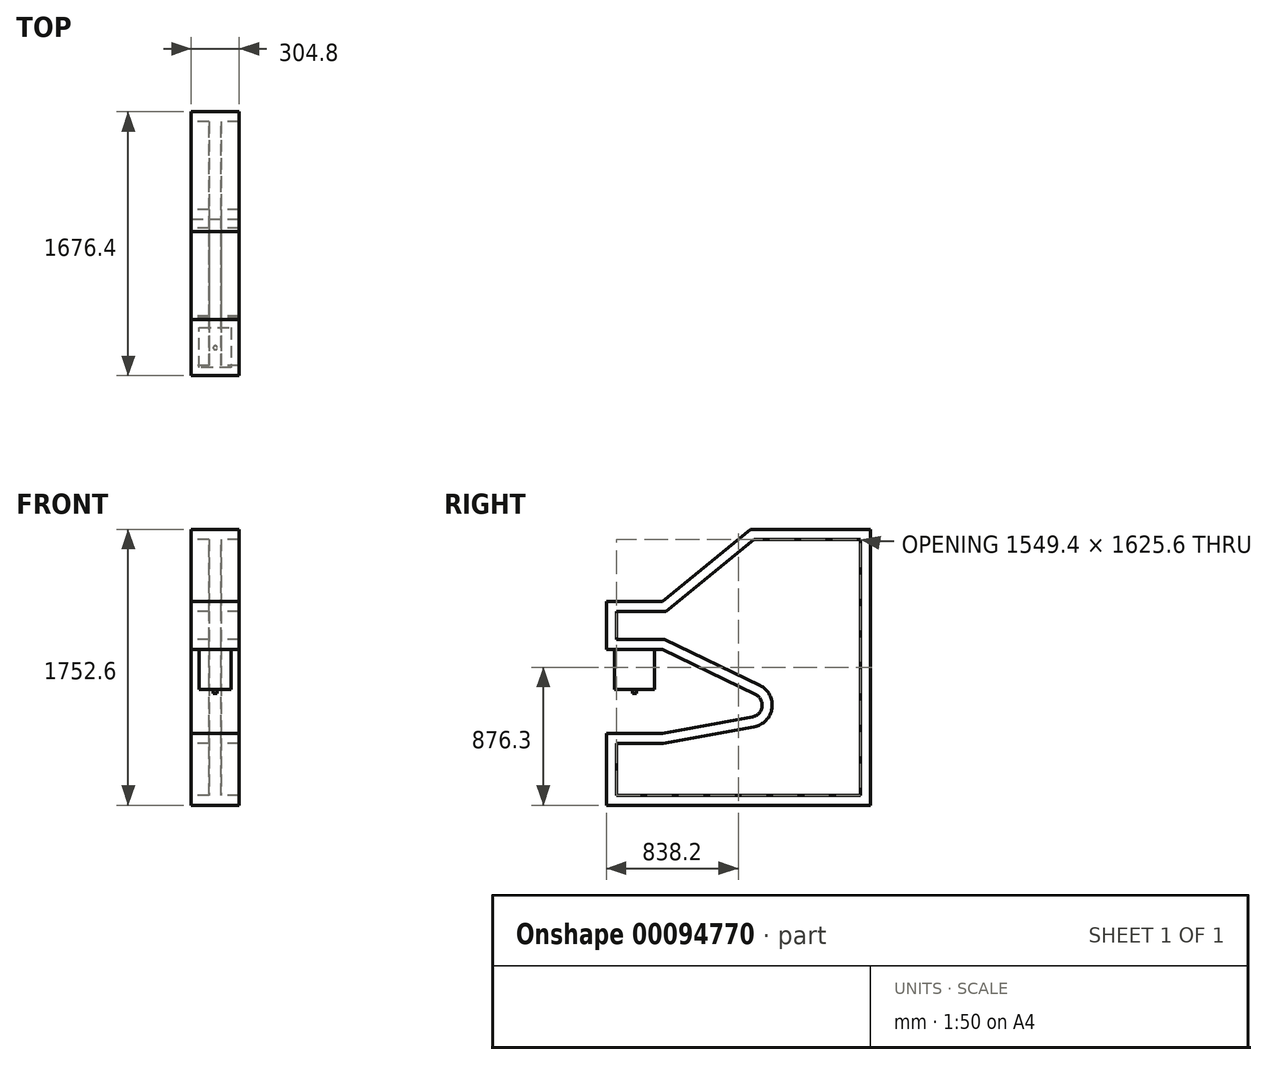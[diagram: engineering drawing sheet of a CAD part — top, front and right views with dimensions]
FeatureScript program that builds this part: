
annotation { "Feature Type Name" : "Feature", "Feature Type Description" : "" }
export const myFeature = defineFeature(function(context is Context, id is Id, definition is map)
    precondition{}
    {
        {
            var Q0;
            Q0=qCreatedBy(makeId("Right.planeOp"),FACE);
            var sketch = newSketch(context, id + "F0", { "sketchPlane" : qUnion([Q0])});
            skLineSegment(sketch, "E0", {"start": v(-914.4, 0) * mm, "end": v(762, 0) * mm, "construction": true});
            skLineSegment(sketch, "E1.0", {"start": v(-914.4, 457.2) * mm, "end": v(0, 457.2) * mm, "construction": true});
            skLineSegment(sketch, "E2.0", {"start": v(-1354.22, 635) * mm, "end": v(1358.95, 635) * mm, "construction": true});
            skLineSegment(sketch, "E3.0", {"start": v(-914.4, 990.6) * mm, "end": v(0, 990.6) * mm, "construction": true});
            skLineSegment(sketch, "E4.0", {"start": v(-914.4, 1295.4) * mm, "end": v(0, 1295.4) * mm, "construction": true});
            skLineSegment(sketch, "E5", {"start": v(-914.4, 1295.4) * mm, "end": v(-914.4, 0) * mm, "construction": true});
            skLineSegment(sketch, "E6.0", {"start": v(-558.8, 1295.4) * mm, "end": v(-558.8, 0) * mm, "construction": true});
            skLineSegment(sketch, "E7.0", {"start": v(-1354.22, 1752.6) * mm, "end": v(1358.95, 1752.6) * mm, "construction": true});
            skLineSegment(sketch, "E8", {"start": v(0, -258.78) * mm, "end": v(0, 1895.33) * mm, "construction": true});
            skLineSegment(sketch, "E9.0", {"start": v(762, -258.78) * mm, "end": v(762, 1895.33) * mm, "construction": true});
            skArc(sketch, "E10", {"start": v(13.47, 560) * mm, "mid": v(75.49, 624.6) * mm, "end": v(33.24, 703.57) * mm});
            skLineSegment(sketch, "E11", {"start": v(-558.8, 990.6) * mm, "end": v(33.24, 703.57) * mm});
            skLineSegment(sketch, "E12", {"start": v(-558.8, 457.2) * mm, "end": v(13.47, 560) * mm});
            skLineSegment(sketch, "E13", {"start": v(-558.8, 990.6) * mm, "end": v(-914.4, 990.6) * mm});
            skLineSegment(sketch, "E14", {"start": v(-914.4, 990.6) * mm, "end": v(-914.4, 1295.4) * mm});
            skLineSegment(sketch, "E15", {"start": v(-914.4, 1295.4) * mm, "end": v(-558.8, 1295.4) * mm});
            skLineSegment(sketch, "E16", {"start": v(-558.8, 1295.4) * mm, "end": v(0, 1752.6) * mm});
            skLineSegment(sketch, "E17", {"start": v(0, 1752.6) * mm, "end": v(762, 1752.6) * mm});
            skLineSegment(sketch, "E18", {"start": v(762, 1752.6) * mm, "end": v(762, 0) * mm});
            skLineSegment(sketch, "E19", {"start": v(-914.4, 0) * mm, "end": v(762, 0) * mm});
            skLineSegment(sketch, "E20", {"start": v(-914.4, 0) * mm, "end": v(-914.4, 457.2) * mm});
            skLineSegment(sketch, "E21", {"start": v(-914.4, 457.2) * mm, "end": v(-558.8, 457.2) * mm});
            skPoint(sketch, "E22.orphan", {"position": v(0, 557.58) * mm});
            skSolve(sketch);
        }
        {
            var Q0;
            Q0=qSketchRegion(id+"F0",true);
            extrude(context, id + "F1", {"entities" : qUnion([Q0]), "endBound" : BoundingType.SYMMETRIC, "depth" : 76.2 * mm});
        }
        {
            var Q0;
            Q0=qCreatedBy(makeId("Right.planeOp"),FACE);
            var sketch = newSketch(context, id + "F2", { "sketchPlane" : qUnion([Q0])});
            skArc(sketch, "E23.0.0", {"start": v(33.24, 703.57) * mm, "mid": v(75.49, 624.6) * mm, "end": v(13.47, 560) * mm});
            skLineSegment(sketch, "E23.0.1", {"start": v(13.47, 560) * mm, "end": v(-558.8, 457.2) * mm});
            skLineSegment(sketch, "E23.0.2", {"start": v(-558.8, 457.2) * mm, "end": v(-914.4, 457.2) * mm});
            skLineSegment(sketch, "E23.0.3", {"start": v(-914.4, 457.2) * mm, "end": v(-914.4, 0) * mm});
            skLineSegment(sketch, "E23.0.4", {"start": v(-914.4, 0) * mm, "end": v(762, 0) * mm});
            skLineSegment(sketch, "E23.0.5", {"start": v(762, 0) * mm, "end": v(762, 1752.6) * mm});
            skLineSegment(sketch, "E23.0.6", {"start": v(762, 1752.6) * mm, "end": v(0, 1752.6) * mm});
            skLineSegment(sketch, "E23.0.7", {"start": v(0, 1752.6) * mm, "end": v(-558.8, 1295.4) * mm});
            skLineSegment(sketch, "E23.0.8", {"start": v(-558.8, 1295.4) * mm, "end": v(-914.4, 1295.4) * mm});
            skLineSegment(sketch, "E23.0.9", {"start": v(-914.4, 1295.4) * mm, "end": v(-914.4, 990.6) * mm});
            skLineSegment(sketch, "E23.0.10", {"start": v(-914.4, 990.6) * mm, "end": v(-558.8, 990.6) * mm});
            skLineSegment(sketch, "E23.0.11", {"start": v(-558.8, 990.6) * mm, "end": v(33.24, 703.57) * mm});
            skLineSegment(sketch, "E24.0", {"start": v(698.5, 63.5) * mm, "end": v(698.5, 1689.1) * mm});
            skLineSegment(sketch, "E24.1", {"start": v(-850.9, 1054.1) * mm, "end": v(-544.22, 1054.1) * mm});
            skLineSegment(sketch, "E24.2", {"start": v(-850.9, 1231.9) * mm, "end": v(-850.9, 1054.1) * mm});
            skLineSegment(sketch, "E24.3", {"start": v(-536.13, 1231.9) * mm, "end": v(-850.9, 1231.9) * mm});
            skLineSegment(sketch, "E24.4", {"start": v(22.67, 1689.1) * mm, "end": v(-536.13, 1231.9) * mm});
            skLineSegment(sketch, "E24.5", {"start": v(-544.22, 1054.1) * mm, "end": v(60.94, 760.7) * mm});
            skLineSegment(sketch, "E24.6", {"start": v(698.5, 1689.1) * mm, "end": v(22.67, 1689.1) * mm});
            skArc(sketch, "E24.7", {"start": v(60.94, 760.7) * mm, "mid": v(138.4, 615.94) * mm, "end": v(24.7, 497.5) * mm});
            skLineSegment(sketch, "E24.8", {"start": v(24.7, 497.5) * mm, "end": v(-553.14, 393.7) * mm});
            skLineSegment(sketch, "E24.9", {"start": v(-553.14, 393.7) * mm, "end": v(-850.9, 393.7) * mm});
            skLineSegment(sketch, "E24.10", {"start": v(-850.9, 393.7) * mm, "end": v(-850.9, 63.5) * mm});
            skLineSegment(sketch, "E24.11", {"start": v(-850.9, 63.5) * mm, "end": v(698.5, 63.5) * mm});
            skSolve(sketch);
        }
        {
            var Q0;
            Q0=qSketchRegion(id+"F2",true);
            extrude(context, id + "F3", {"entities" : qUnion([Q0]), "endBound" : BoundingType.SYMMETRIC, "depth" : 304.8 * mm});
        }
        {
            var Q0;
            Q0=makeQuery(id+"F1.opExtrude","SWEPT_BODY",BODY,{"disambiguationData":[OSD([sQuery(id+"F0.wireOp",EDGE,"E10"),sQuery(id+"F0.wireOp",EDGE,"E11"),sQuery(id+"F0.wireOp",EDGE,"E12"),sQuery(id+"F0.wireOp",EDGE,"E13"),sQuery(id+"F0.wireOp",EDGE,"E14"),sQuery(id+"F0.wireOp",EDGE,"E15"),sQuery(id+"F0.wireOp",EDGE,"E16"),sQuery(id+"F0.wireOp",EDGE,"E17"),sQuery(id+"F0.wireOp",EDGE,"E18"),sQuery(id+"F0.wireOp",EDGE,"E19"),sQuery(id+"F0.wireOp",EDGE,"E20"),sQuery(id+"F0.wireOp",EDGE,"E21")])]});
            var Q1;
            Q1=makeQuery(id+"F3.opExtrude","SWEPT_BODY",BODY,{"disambiguationData":[OSD([sQuery(id+"F2.wireOp",EDGE,"E23.0.0"),sQuery(id+"F2.wireOp",EDGE,"E23.0.1"),sQuery(id+"F2.wireOp",EDGE,"E23.0.2"),sQuery(id+"F2.wireOp",EDGE,"E23.0.3"),sQuery(id+"F2.wireOp",EDGE,"E23.0.4"),sQuery(id+"F2.wireOp",EDGE,"E23.0.5"),sQuery(id+"F2.wireOp",EDGE,"E23.0.6"),sQuery(id+"F2.wireOp",EDGE,"E23.0.7"),sQuery(id+"F2.wireOp",EDGE,"E23.0.8"),sQuery(id+"F2.wireOp",EDGE,"E23.0.9"),sQuery(id+"F2.wireOp",EDGE,"E23.0.10"),sQuery(id+"F2.wireOp",EDGE,"E23.0.11"),sQuery(id+"F2.wireOp",EDGE,"E24.0"),sQuery(id+"F2.wireOp",EDGE,"E24.1"),sQuery(id+"F2.wireOp",EDGE,"E24.2"),sQuery(id+"F2.wireOp",EDGE,"E24.3"),sQuery(id+"F2.wireOp",EDGE,"E24.4"),sQuery(id+"F2.wireOp",EDGE,"E24.5"),sQuery(id+"F2.wireOp",EDGE,"E24.6"),sQuery(id+"F2.wireOp",EDGE,"E24.7"),sQuery(id+"F2.wireOp",EDGE,"E24.8"),sQuery(id+"F2.wireOp",EDGE,"E24.9"),sQuery(id+"F2.wireOp",EDGE,"E24.10"),sQuery(id+"F2.wireOp",EDGE,"E24.11")])]});
            booleanBodies(context, id + "F4", {"operationType" : BooleanOperationType.UNION, "tools" : qUnion([Q0, Q1])});
        }
        {
            var Q0;
            Q0=makeQuery(id+"F4.opBoolean","MERGE",FACE,{"derivedFrom":[makeQuery(id+"F1.opExtrude","SWEPT_FACE",FACE,{"disambiguationData":[OSD([sQuery(id+"F0.wireOp",EDGE,"E13")])]}),makeQuery(id+"F3.opExtrude","SWEPT_FACE",FACE,{"disambiguationData":[OSD([sQuery(id+"F2.wireOp",EDGE,"E23.0.10")])]})]});
            var sketch = newSketch(context, id + "F5", { "sketchPlane" : qUnion([Q0])});
            skLineSegment(sketch, "E25.0.0", {"start": v(152.4, 914.4) * mm, "end": v(-152.4, 914.4) * mm});
            skLineSegment(sketch, "E25.0.1", {"start": v(-152.4, 914.4) * mm, "end": v(-152.4, 558.8) * mm});
            skLineSegment(sketch, "E25.0.2", {"start": v(-152.4, 558.8) * mm, "end": v(152.4, 558.8) * mm});
            skLineSegment(sketch, "E25.0.3", {"start": v(152.4, 558.8) * mm, "end": v(152.4, 914.4) * mm});
            skLineSegment(sketch, "E26.0", {"start": v(101.6, 863.6) * mm, "end": v(-101.6, 863.6) * mm});
            skLineSegment(sketch, "E26.1", {"start": v(101.6, 609.6) * mm, "end": v(101.6, 863.6) * mm});
            skLineSegment(sketch, "E26.2", {"start": v(-101.6, 609.6) * mm, "end": v(101.6, 609.6) * mm});
            skLineSegment(sketch, "E26.3", {"start": v(-101.6, 863.6) * mm, "end": v(-101.6, 609.6) * mm});
            skSolve(sketch);
        }
        {
            var Q0;
            Q0=makeQuery(id+"F5.imprint","IMPRINT",FACE,{"disambiguationData":[TD([[makeQuery(id+"F5.imprint","IMPRINT",EDGE,{"derivedFrom":sQuery(id+"F5.wireOp",EDGE,"E26.0")}),1.0]])]});
            extrude(context, id + "F6", {"entities" : qUnion([Q0]), "operationType" : NewBodyOperationType.ADD, "depth" : 254 * mm});
        }
        {
            var Q0;
            Q0=makeQuery(id+"F6.opExtrude","CAP_FACE",FACE,{"disambiguationData":[OSD([sQuery(id+"F5.wireOp",EDGE,"E26.0"),sQuery(id+"F5.wireOp",EDGE,"E26.1"),sQuery(id+"F5.wireOp",EDGE,"E26.2"),sQuery(id+"F5.wireOp",EDGE,"E26.3")])],"isStart":false});
            var sketch = newSketch(context, id + "F7", { "sketchPlane" : qUnion([Q0])});
            skLineSegment(sketch, "E27", {"start": v(101.6, 863.6) * mm, "end": v(-101.6, 609.6) * mm, "construction": true});
            skCircle(sketch, "E28", {"center": v(0, 736.6) * mm, "radius": 12.7 * mm});
            skSolve(sketch);
        }
        {
            var Q0;
            Q0 = qSketchRegion(id + "F7", true);
            extrude(context, id + "F8", {"entities" : qUnion([Q0]), "operationType" : NewBodyOperationType.ADD, "depth" : 25.4 * mm});
        }
    });
